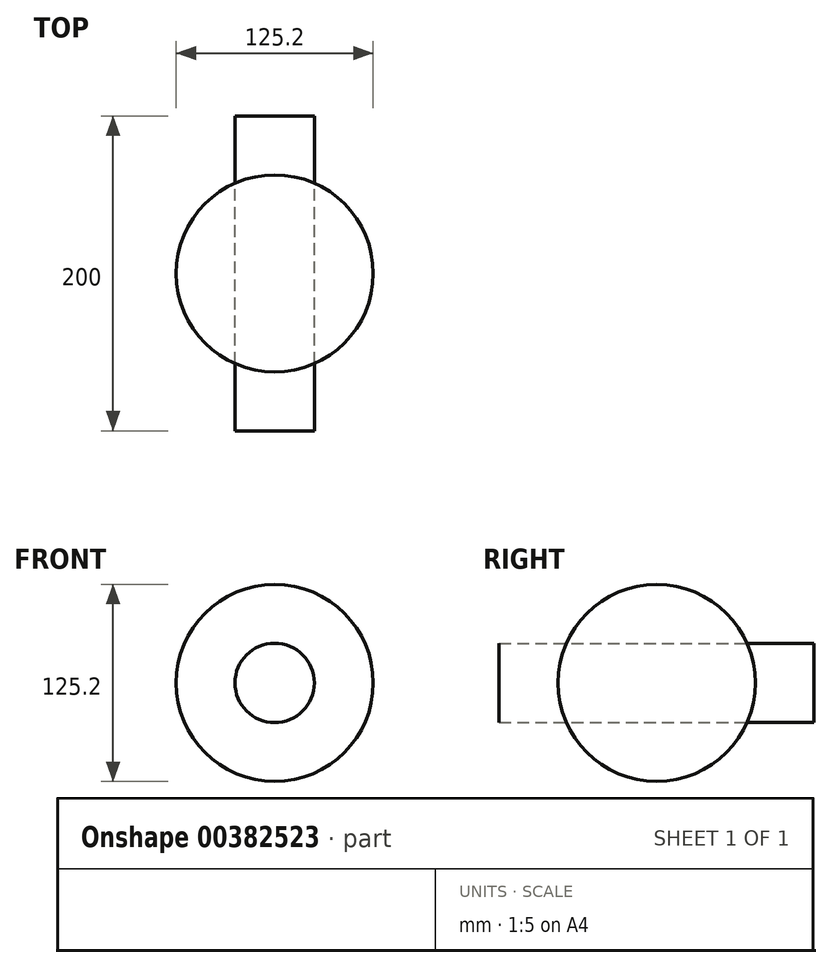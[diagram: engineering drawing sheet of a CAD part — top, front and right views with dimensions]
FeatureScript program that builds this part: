
annotation { "Feature Type Name" : "Feature", "Feature Type Description" : "" }
export const myFeature = defineFeature(function(context is Context, id is Id, definition is map)
    precondition{}
    {
        {
            var Q0;
            Q0=qCreatedBy(makeId("Front.planeOp"),FACE);
            var sketch = newSketch(context, id + "F0", { "sketchPlane" : qUnion([Q0])});
            skArc(sketch, "E0", {"start": v(0, -62.6) * mm, "mid": v(62.6, 0) * mm, "end": v(0, 62.6) * mm});
            skLineSegment(sketch, "E1", {"start": v(0, 0) * mm, "end": v(0, 62.6) * mm});
            skLineSegment(sketch, "E2", {"start": v(0, 62.6) * mm, "end": v(0, -62.6) * mm});
            skSolve(sketch);
        }
        {
            var Q0;
            {var subQ0=sQuery(id+"F0.wireOp",EDGE,"E0");Q0=makeQuery(id+"F0.imprint","IMPRINT",FACE,{"disambiguationData":[TD([[makeQuery(id+"F0.imprint","IMPRINT",EDGE,{"derivedFrom":subQ0}),1.0]])]});}
            var Q1;
            Q1=sQuery(id+"F0.wireOp",EDGE,"E2");
            revolve(context, id + "F1", {"entities" : qUnion([Q0]), "axis" : qUnion([Q1]), "revolveType" : RevolveType.FULL});
        }
        {
            var Q0;
            Q0=qCreatedBy(makeId("Front.planeOp"),FACE);
            var sketch = newSketch(context, id + "F2", { "sketchPlane" : qUnion([Q0])});
            skCircle(sketch, "E3", {"center": v(0, 0) * mm, "radius": 25.2 * mm});
            skSolve(sketch);
        }
        {
            var Q0;
            Q0 = qSketchRegion(id + "F2", true);
            extrude(context, id + "F3", {"entities" : qUnion([Q0]), "endBound" : BoundingType.SYMMETRIC, "depth" : 200 * mm});
        }
    });
